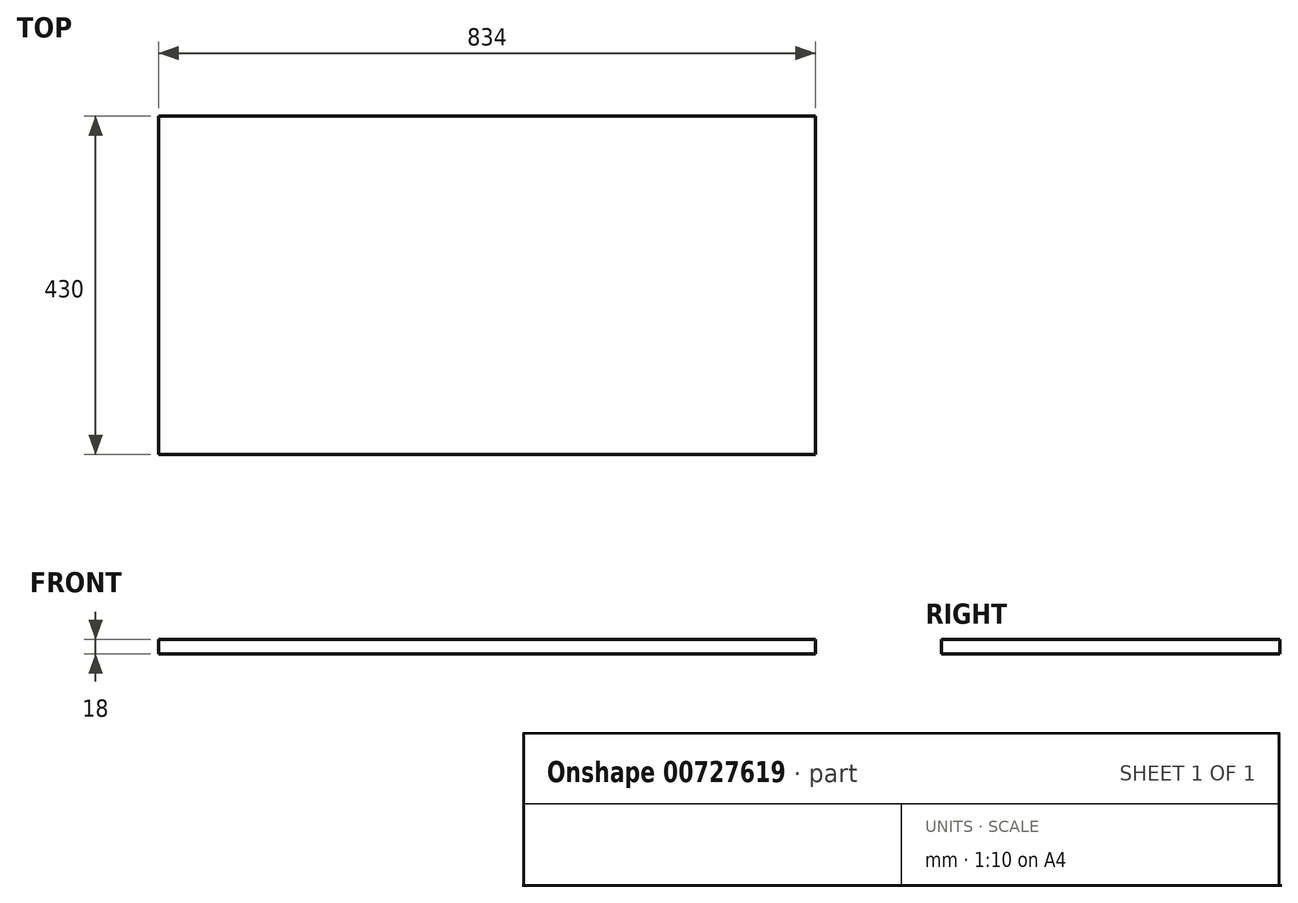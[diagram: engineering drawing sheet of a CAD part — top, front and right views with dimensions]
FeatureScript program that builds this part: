
annotation { "Feature Type Name" : "Feature", "Feature Type Description" : "" }
export const myFeature = defineFeature(function(context is Context, id is Id, definition is map)
    precondition{}
    {
        {
            var Q0;
            Q0=qCreatedBy(makeId("Top.planeOp"),FACE);
            var sketch = newSketch(context, id + "F0", { "sketchPlane" : qUnion([Q0])});
            skLineSegment(sketch, "E0.bottom", {"start": v(-417, -215) * mm, "end": v(417, -215) * mm});
            skLineSegment(sketch, "E0.top", {"start": v(-417, 215) * mm, "end": v(417, 215) * mm});
            skLineSegment(sketch, "E0.left", {"start": v(-417, -215) * mm, "end": v(-417, 215) * mm});
            skLineSegment(sketch, "E0.right", {"start": v(417, -215) * mm, "end": v(417, 215) * mm});
            skPoint(sketch, "E0.middle", {"position": v(0, 0) * mm});
            skSolve(sketch);
        }
        {
            var Q0;
            Q0 = qSketchRegion(id + "F0", true);
            extrude(context, id + "F1", {"entities" : qUnion([Q0]), "depth" : 18 * mm, "offsetDistance" : 25 * mm});
        }
    });
